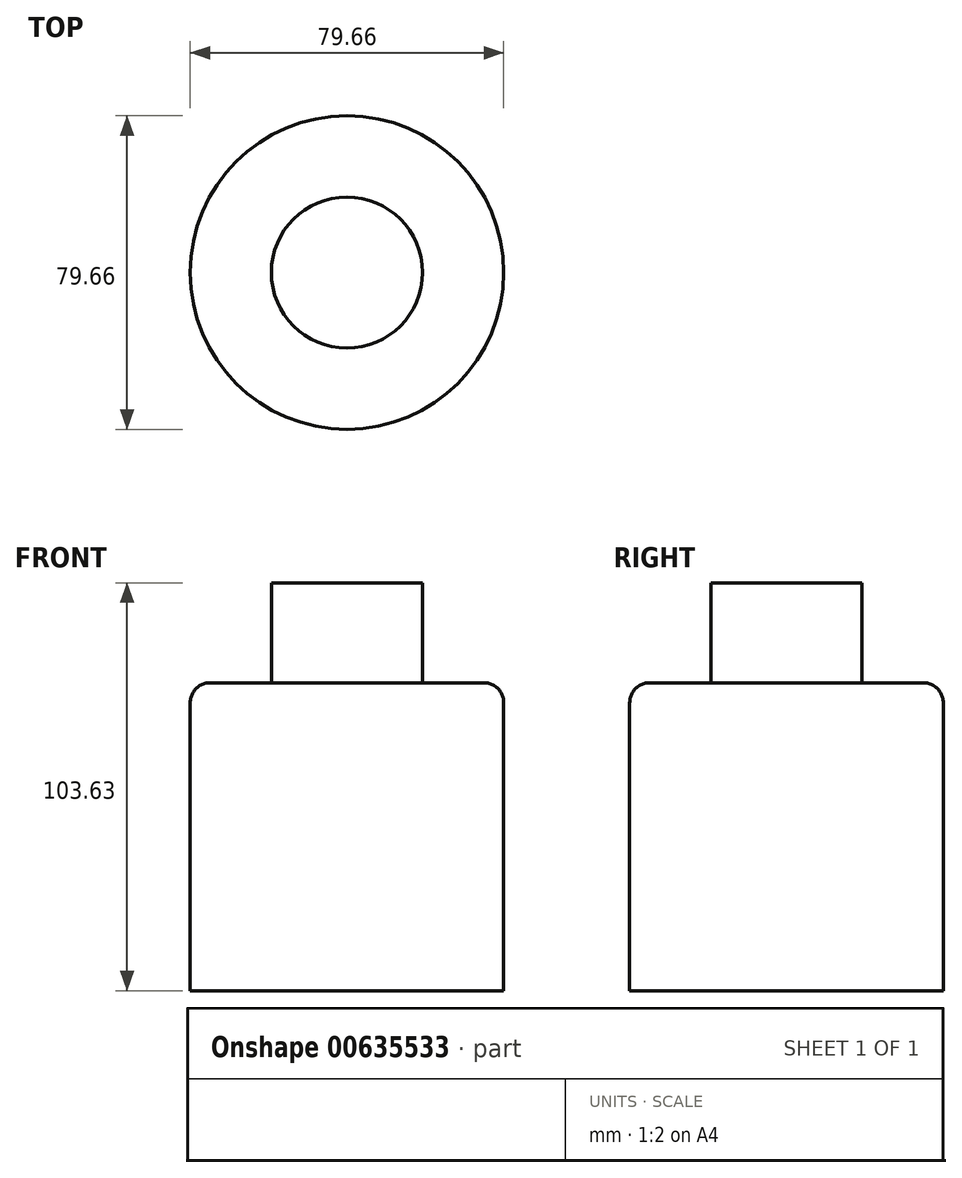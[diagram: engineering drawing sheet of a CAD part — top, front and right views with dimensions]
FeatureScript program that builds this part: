
annotation { "Feature Type Name" : "Feature", "Feature Type Description" : "" }
export const myFeature = defineFeature(function(context is Context, id is Id, definition is map)
    precondition{}
    {
        {
            var Q0;
            Q0=qCreatedBy(makeId("Top.planeOp"),FACE);
            var sketch = newSketch(context, id + "F0", { "sketchPlane" : qUnion([Q0])});
            skCircle(sketch, "E0", {"center": v(0, 0) * mm, "radius": 39.83 * mm});
            skSolve(sketch);
        }
        {
            var Q0;
            Q0=makeQuery(id+"F0.imprint","IMPRINT",FACE,{"disambiguationData":[TD([[makeQuery(id+"F0.imprint","IMPRINT",EDGE,{"derivedFrom":sQuery(id+"F0.wireOp",EDGE,"E0")}),1.0]])]});
            extrude(context, id + "F1", {"entities" : qUnion([Q0]), "depth" : 78.23 * mm, "offsetDistance" : 25.4 * mm});
        }
        {
            var Q0;
            Q0=makeQuery(id+"F1.opExtrude","CAP_EDGE",EDGE,{"disambiguationData":[OSD([sQuery(id+"F0.wireOp",EDGE,"E0")])],"isStart":false});
            fillet(context, id + "F2", {"entities" : qUnion([Q0]), "radius" : 5.08 * mm, "tangentPropagation" : true, "allowEdgeOverflow" : false});
        }
        {
            var Q0;
            Q0=makeQuery(id+"F1.opExtrude","CAP_FACE",FACE,{"disambiguationData":[OSD([sQuery(id+"F0.wireOp",EDGE,"E0")])],"isStart":false});
            var sketch = newSketch(context, id + "F3", { "sketchPlane" : qUnion([Q0])});
            skCircle(sketch, "E1", {"center": v(0, 0) * mm, "radius": 19.2 * mm});
            skSolve(sketch);
        }
        {
            var Q0;
            Q0=makeQuery(id+"F3.imprint","IMPRINT",FACE,{"disambiguationData":[TD([[makeQuery(id+"F3.imprint","IMPRINT",EDGE,{"derivedFrom":sQuery(id+"F3.wireOp",EDGE,"E1")}),1.0]])]});
            extrude(context, id + "F4", {"entities" : qUnion([Q0]), "operationType" : NewBodyOperationType.ADD, "depth" : 25.4 * mm, "offsetDistance" : 25.4 * mm});
        }
    });
